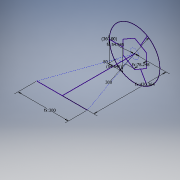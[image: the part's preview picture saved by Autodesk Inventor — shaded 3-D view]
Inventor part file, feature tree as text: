
AUTODESK INVENTOR PART (.ipt)
format: ipt  version: 2016 (Build 200138000, 138)  size: 97,792 bytes
history: native  units: mm
features: sketch x2
ambient origin geometry x8: Origin, YZ Plane, XZ Plane, XY Plane, X Axis, Y Axis, Z Axis, Center Point
feature tree (2):
  sketch  "Sketch1"  dims[d1=30.0mm d3=360.0deg]
  sketch  "Sketch2"  dims[d5=80.0mm d6=430.364mm d7=300.0mm d8=78.248mm d11=54.545455mm]
